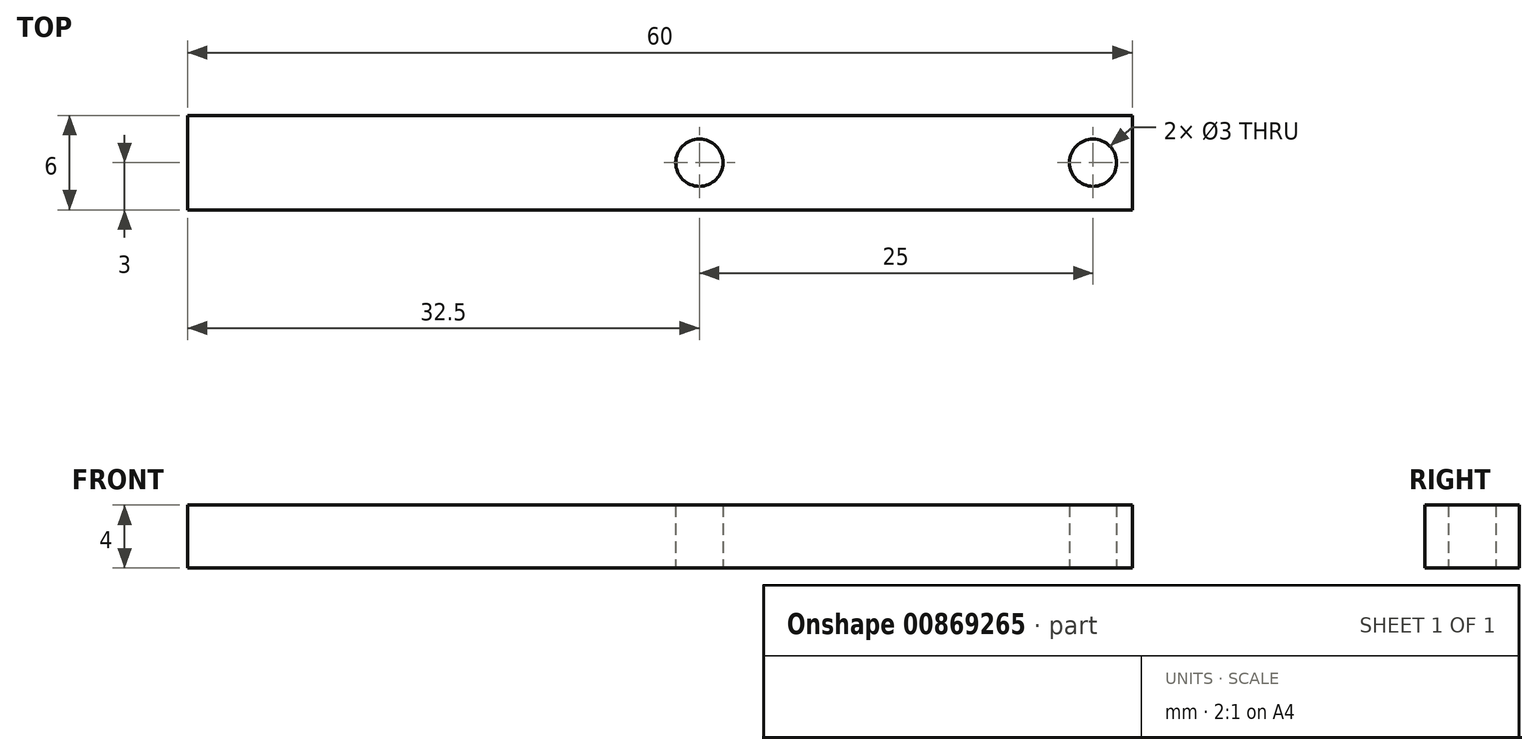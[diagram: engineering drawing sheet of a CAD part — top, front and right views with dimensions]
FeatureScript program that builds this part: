
annotation { "Feature Type Name" : "Feature", "Feature Type Description" : "" }
export const myFeature = defineFeature(function(context is Context, id is Id, definition is map)
    precondition{}
    {
        {
            var Q0;
            Q0=qCreatedBy(makeId("Top.planeOp"),FACE);
            var sketch = newSketch(context, id + "F0", { "sketchPlane" : qUnion([Q0])});
            skLineSegment(sketch, "E0.bottom", {"start": v(42.5, -3) * mm, "end": v(-17.5, -3) * mm});
            skLineSegment(sketch, "E0.top", {"start": v(42.5, 3) * mm, "end": v(-17.5, 3) * mm});
            skLineSegment(sketch, "E0.left", {"start": v(42.5, -3) * mm, "end": v(42.5, 3) * mm});
            skLineSegment(sketch, "E0.right", {"start": v(-17.5, -3) * mm, "end": v(-17.5, 3) * mm});
            skPoint(sketch, "E0.middle", {"position": v(0, 0) * mm});
            skLineSegment(sketch, "E1.bottom", {"start": v(-17.5, 0) * mm, "end": v(42.5, 0) * mm, "construction": true});
            skLineSegment(sketch, "E1.top", {"start": v(-17.5, -3) * mm, "end": v(42.5, -3) * mm});
            skLineSegment(sketch, "E1.left", {"start": v(-17.5, 0) * mm, "end": v(-17.5, -3) * mm});
            skLineSegment(sketch, "E1.right", {"start": v(42.5, 0) * mm, "end": v(42.5, -3) * mm});
            skLineSegment(sketch, "E2.bottom", {"start": v(15, 0) * mm, "end": v(40, 0) * mm, "construction": true});
            skLineSegment(sketch, "E3", {"start": v(-15, 0) * mm, "end": v(-5, 0) * mm});
            skLineSegment(sketch, "E4", {"start": v(15, 0) * mm, "end": v(-17.5, 0) * mm, "construction": true});
            skSolve(sketch);
        }
        {
            var Q0;
            Q0=makeQuery(id+"F0.imprint","IMPRINT",FACE,{"disambiguationData":[TD([[makeQuery(id+"F0.imprint","IMPRINT",EDGE,{"derivedFrom":sQuery(id+"F0.wireOp",EDGE,"E0.top")}),1.0]])]});
            extrude(context, id + "F1", {"entities" : qUnion([Q0]), "depth" : 4 * mm, "offsetDistance" : 25 * mm});
        }
        {
            var Q0;
            Q0=sQuery(id+"F0.wireOp",VERTEX,"uNmYuHKQ-gdCR-IE9V-lbN0-rti3GN8YhHF9.top.end");
            var Q1;
            Q1=sQuery(id+"F0.wireOp",VERTEX,"uNmYuHKQ-gdCR-IE9V-lbN0-rti3GN8YhHF9.bottom.start");
            var Q2;
            Q2=sQuery(id+"F0.wireOp",VERTEX,"E2.bottom.end");
            var Q3;
            Q3=sQuery(id+"F0.wireOp",VERTEX,"uNmYuHKQ-gdCR-IE9V-lbN0-rti3GN8YhHF9.top.start");
            var Q4;
            Q4=sQuery(id+"F0.wireOp",VERTEX,"E2.bottom.start");
            var Q5;
            Q5=makeQuery(id+"F1.opExtrude","SWEPT_BODY",BODY,{"disambiguationData":[OSD([sQuery(id+"F0.wireOp",EDGE,"E0.top"),sQuery(id+"F0.wireOp",EDGE,"E0.left"),sQuery(id+"F0.wireOp",EDGE,"E0.right"),sQuery(id+"F0.wireOp",EDGE,"E1.top"),sQuery(id+"F0.wireOp",EDGE,"E1.left"),sQuery(id+"F0.wireOp",EDGE,"E1.right")])]});
            hole(context, id + "F2", {"style" : HoleStyle.SIMPLE, "endStyle" : HoleEndStyle.THROUGH, "oppositeDirection" : true, "holeDiameter" : 3 * mm, "majorDiameter" : 5 * mm, "isTappedThrough" : true, "tappedDepth" : 12 * mm, "tapClearance" : 3, "locations" : qUnion([Q0, Q1, Q2, Q3, Q4]), "scope" : qUnion([Q5])});
        }
    });
